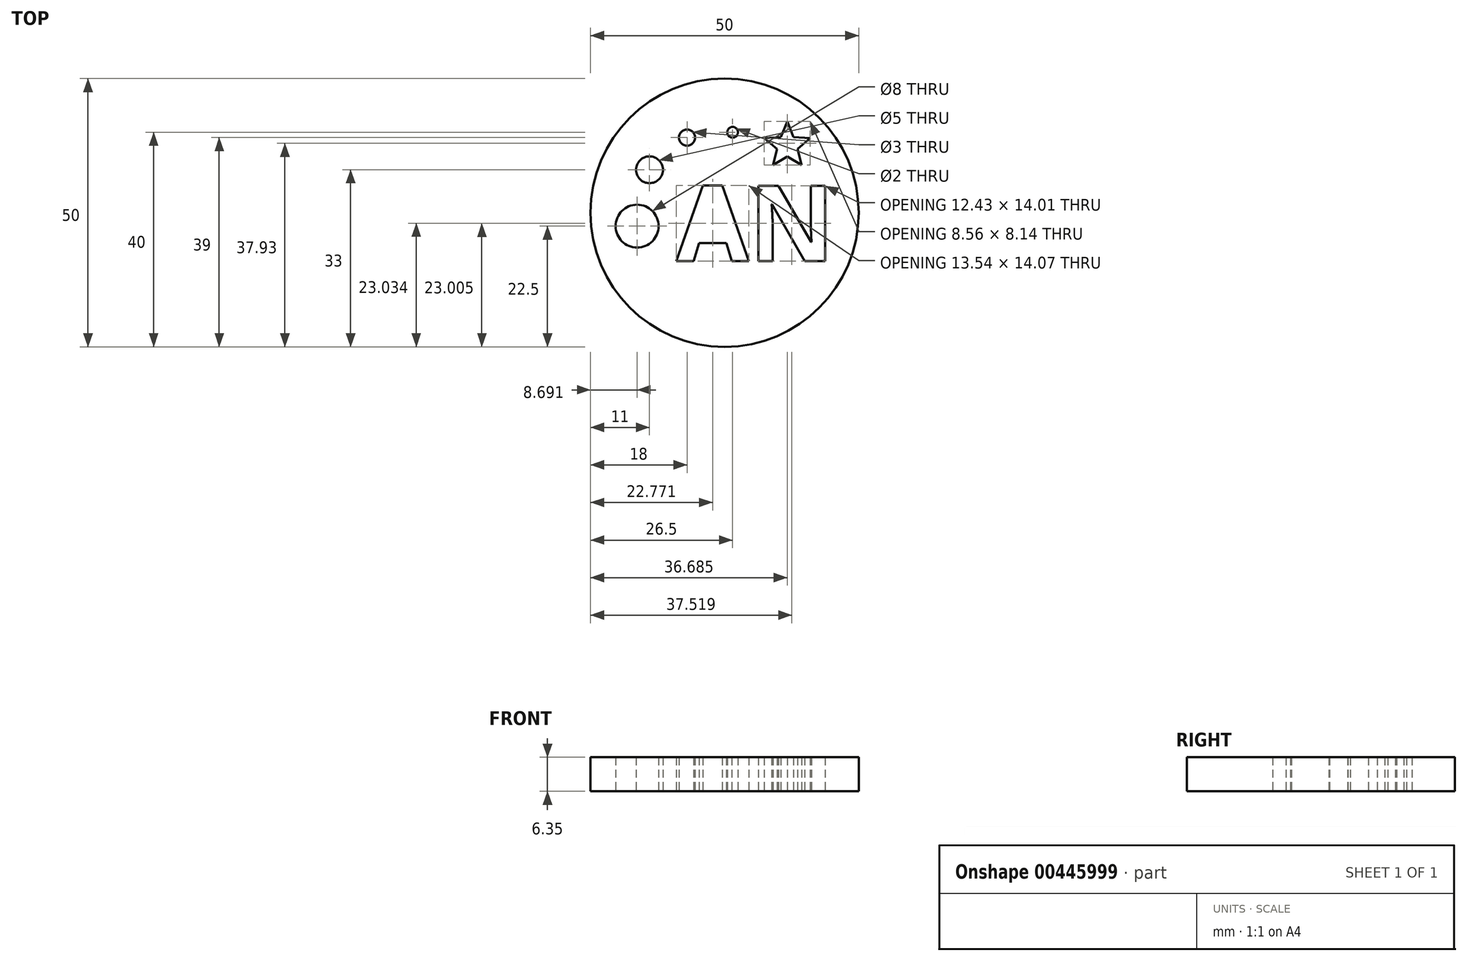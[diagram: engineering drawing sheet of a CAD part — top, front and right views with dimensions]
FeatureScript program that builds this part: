
annotation { "Feature Type Name" : "Feature", "Feature Type Description" : "" }
export const myFeature = defineFeature(function(context is Context, id is Id, definition is map)
    precondition{}
    {
        {
            var Q0;
            Q0=qCreatedBy(makeId("Top.planeOp"),FACE);
            var sketch = newSketch(context, id + "F0", { "sketchPlane" : qUnion([Q0])});
            skText(sketch, "E0", { "text": "AN", "fontName": "OpenSans-Bold.ttf"});
            skPoint(sketch, "E1", {"position": v(-16.3, -2.5) * mm});
            skPoint(sketch, "E2.1.0", {"position": v(-14, 8) * mm});
            skPoint(sketch, "E2.2.0", {"position": v(-7, 14) * mm});
            skPoint(sketch, "E2.3.0", {"position": v(1.5, 15) * mm});
            skCircle(sketch, "E3", {"center": v(-16.3, -2.5) * mm, "radius": 4 * mm});
            skCircle(sketch, "E4", {"center": v(-14, 8) * mm, "radius": 2.5 * mm});
            skCircle(sketch, "E5", {"center": v(-7, 14) * mm, "radius": 1.5 * mm});
            skPoint(sketch, "E6", {"position": v(11.69, 17) * mm});
            skPoint(sketch, "E7.1.0", {"position": v(7.4, 13.9) * mm});
            skPoint(sketch, "E7.2.0", {"position": v(9.04, 8.86) * mm});
            skPoint(sketch, "E7.3.0", {"position": v(14.33, 8.86) * mm});
            skPoint(sketch, "E7.4.0", {"position": v(15.96, 13.9) * mm});
            skPoint(sketch, "E7.center", {"position": v(11.69, 12.5) * mm});
            skPoint(sketch, "E8", {"position": v(11.69, 10.5) * mm});
            skPoint(sketch, "E9.1.0", {"position": v(13.59, 11.88) * mm});
            skPoint(sketch, "E9.2.0", {"position": v(12.86, 14.12) * mm});
            skPoint(sketch, "E9.3.0", {"position": v(10.5, 14.12) * mm});
            skPoint(sketch, "E9.4.0", {"position": v(9.78, 11.88) * mm});
            skLineSegment(sketch, "E10", {"start": v(11.69, 17) * mm, "end": v(10.5, 14.12) * mm});
            skLineSegment(sketch, "E11", {"start": v(10.5, 14.12) * mm, "end": v(7.4, 13.9) * mm});
            skLineSegment(sketch, "E12", {"start": v(7.4, 13.9) * mm, "end": v(9.78, 11.88) * mm});
            skLineSegment(sketch, "E13", {"start": v(9.78, 11.88) * mm, "end": v(9.04, 8.86) * mm});
            skLineSegment(sketch, "E14", {"start": v(9.04, 8.86) * mm, "end": v(11.69, 10.5) * mm});
            skLineSegment(sketch, "E15", {"start": v(11.69, 10.5) * mm, "end": v(14.33, 8.86) * mm});
            skLineSegment(sketch, "E16", {"start": v(14.33, 8.86) * mm, "end": v(13.59, 11.88) * mm});
            skLineSegment(sketch, "E17", {"start": v(13.59, 11.88) * mm, "end": v(15.96, 13.9) * mm});
            skLineSegment(sketch, "E18", {"start": v(15.96, 13.9) * mm, "end": v(12.86, 14.12) * mm});
            skLineSegment(sketch, "E19", {"start": v(12.86, 14.12) * mm, "end": v(11.69, 17) * mm});
            skCircle(sketch, "E20", {"center": v(1.5, 15) * mm, "radius": 1 * mm});
            skPoint(sketch, "E21", {"position": v(5.5, -1.94) * mm});
            skCircle(sketch, "E22", {"center": v(0, 0) * mm, "radius": 25 * mm});
            skText(sketch, "E23", { "text": "BIOE123", "fontName": "OpenSans-Italic.ttf"});
            const initialGuessF0  = {"E0": [-0.009, -0.009, 1, 0, 0.01413], "E23": [-0.013, -0.01794, 1, 0, 0.00494]};
            skSetInitialGuess(sketch, initialGuessF0);
            skSolve(sketch);
        }
        {
            var Q0;
            Q0=makeQuery(id+"F0.imprint","IMPRINT",FACE,{"disambiguationData":[TD([[makeQuery(id+"F0.imprint","IMPRINT",EDGE,{"derivedFrom":sQuery(id+"F0.wireOp",EDGE,"E0.sketch_text.stroke-0")}),1.0]])]});
            var Q1;
            Q1=makeQuery(id+"F0.imprint","IMPRINT",FACE,{"disambiguationData":[TD([[makeQuery(id+"F0.imprint","IMPRINT",EDGE,{"derivedFrom":sQuery(id+"F0.wireOp",EDGE,"E23.sketch_text.stroke-18")}),1.0]])]});
            var Q2;
            Q2=makeQuery(id+"F0.imprint","IMPRINT",FACE,{"disambiguationData":[TD([[makeQuery(id+"F0.imprint","IMPRINT",EDGE,{"derivedFrom":sQuery(id+"F0.wireOp",EDGE,"E23.sketch_text.stroke-11")}),1.0]])]});
            var Q3;
            Q3=makeQuery(id+"F0.imprint","IMPRINT",FACE,{"disambiguationData":[TD([[makeQuery(id+"F0.imprint","IMPRINT",EDGE,{"derivedFrom":sQuery(id+"F0.wireOp",EDGE,"E23.sketch_text.stroke-0")}),-1.0]])]});
            var Q4;
            Q4=makeQuery(id+"F0.imprint","IMPRINT",FACE,{"disambiguationData":[TD([[makeQuery(id+"F0.imprint","IMPRINT",EDGE,{"derivedFrom":sQuery(id+"F0.wireOp",EDGE,"E23.sketch_text.stroke-25")}),-1.0]])]});
            var Q5;
            Q5=makeQuery(id+"F0.imprint","IMPRINT",FACE,{"disambiguationData":[TD([[makeQuery(id+"F0.imprint","IMPRINT",EDGE,{"derivedFrom":sQuery(id+"F0.wireOp",EDGE,"E23.sketch_text.stroke-29")}),-1.0]])]});
            var Q6;
            Q6=makeQuery(id+"F0.imprint","IMPRINT",FACE,{"disambiguationData":[TD([[makeQuery(id+"F0.imprint","IMPRINT",EDGE,{"derivedFrom":sQuery(id+"F0.wireOp",EDGE,"E23.sketch_text.stroke-39")}),1.0]])]});
            var Q7;
            Q7=makeQuery(id+"F0.imprint","IMPRINT",FACE,{"disambiguationData":[TD([[makeQuery(id+"F0.imprint","IMPRINT",EDGE,{"derivedFrom":sQuery(id+"F0.wireOp",EDGE,"E23.sketch_text.stroke-49")}),-1.0]])]});
            var Q8;
            Q8=makeQuery(id+"F0.imprint","IMPRINT",FACE,{"disambiguationData":[TD([[makeQuery(id+"F0.imprint","IMPRINT",EDGE,{"derivedFrom":sQuery(id+"F0.wireOp",EDGE,"E23.sketch_text.stroke-61")}),-1.0]])]});
            var Q9;
            Q9=makeQuery(id+"F0.imprint","IMPRINT",FACE,{"disambiguationData":[TD([[makeQuery(id+"F0.imprint","IMPRINT",EDGE,{"derivedFrom":sQuery(id+"F0.wireOp",EDGE,"E23.sketch_text.stroke-70")}),-1.0]])]});
            var Q10;
            Q10=makeQuery(id+"F0.imprint","IMPRINT",FACE,{"disambiguationData":[TD([[makeQuery(id+"F0.imprint","IMPRINT",EDGE,{"derivedFrom":sQuery(id+"F0.wireOp",EDGE,"E23.sketch_text.stroke-92")}),-1.0]])]});
            extrude(context, id + "F1", {"entities" : qUnion([Q0, Q1, Q2, Q3, Q4, Q5, Q6, Q7, Q8, Q9, Q10]), "depth" : 6.35 * mm});
        }
    });
